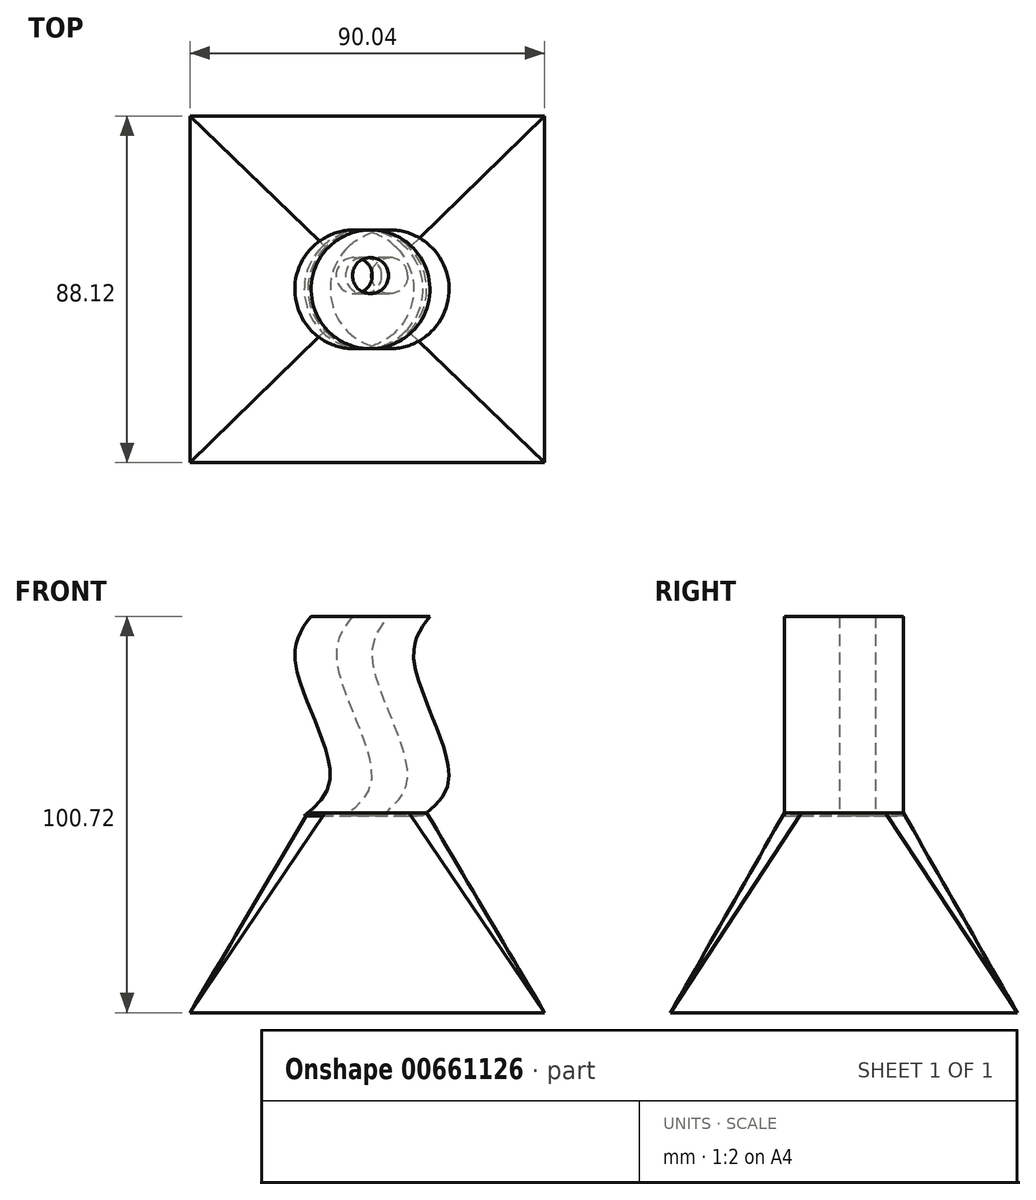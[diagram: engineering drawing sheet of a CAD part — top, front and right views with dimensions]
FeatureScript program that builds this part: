
annotation { "Feature Type Name" : "Feature", "Feature Type Description" : "" }
export const myFeature = defineFeature(function(context is Context, id is Id, definition is map)
    precondition{}
    {
        {
            var Q0;
            Q0=qCreatedBy(makeId("Top.planeOp"),FACE);
            cPlane(context, id + "F0", {"entities" : qUnion([Q0]), "cplaneType" : CPlaneType.OFFSET, "offset" : 50.8 * mm, "width" : 152.4 * mm, "height" : 152.4 * mm});
        }
        {
            var Q0;
            Q0=qCreatedBy(makeId("Top.planeOp"),FACE);
            var sketch = newSketch(context, id + "F1", { "sketchPlane" : qUnion([Q0])});
            skLineSegment(sketch, "E0.bottom", {"start": v(45.02, 44.06) * mm, "end": v(-45.02, 44.06) * mm});
            skLineSegment(sketch, "E0.top", {"start": v(45.02, -44.06) * mm, "end": v(-45.02, -44.06) * mm});
            skLineSegment(sketch, "E0.left", {"start": v(45.02, 44.06) * mm, "end": v(45.02, -44.06) * mm});
            skLineSegment(sketch, "E0.right", {"start": v(-45.02, 44.06) * mm, "end": v(-45.02, -44.06) * mm});
            skPoint(sketch, "E0.middle", {"position": v(0, 0) * mm});
            skSolve(sketch);
        }
        {
            var Q0;
            Q0=qCreatedBy(id+"F0.planeOp",FACE);
            var sketch = newSketch(context, id + "F2", { "sketchPlane" : qUnion([Q0])});
            skCircle(sketch, "E1", {"center": v(0, 0) * mm, "radius": 15.1 * mm});
            skSolve(sketch);
        }
        {
            var Q0;
            Q0=makeQuery(id+"F1.imprint","IMPRINT",FACE,{"disambiguationData":[TD([[makeQuery(id+"F1.imprint","IMPRINT",EDGE,{"derivedFrom":sQuery(id+"F1.wireOp",EDGE,"E0.bottom")}),1.0]])]});
            var Q1;
            Q1=makeQuery(id+"F2.imprint","IMPRINT",FACE,{"disambiguationData":[TD([[makeQuery(id+"F2.imprint","IMPRINT",EDGE,{"derivedFrom":sQuery(id+"F2.wireOp",EDGE,"E1")}),1.0]])]});
            loft(context, id + "F3", {"sheetProfilesArray" : [{ "sheetProfileEntities" : qUnion([Q0]) }, { "sheetProfileEntities" : qUnion([Q1]) }]});
        }
        {
            var Q0;
            Q0=qCreatedBy(makeId("Front.planeOp"),FACE);
            var sketch = newSketch(context, id + "F4", { "sketchPlane" : qUnion([Q0])});
            skFitSpline(sketch, "E2", {"points": [v(0, 50.04) * mm, v(6.6, 60.36) * mm, v(-2.32, 89.52) * mm, v(1.74, 100.72) * mm], "startDerivative": vector(35.2, 28.9) * mm, "endDerivative": vector(24.91, 33.2) * mm});
            skSolve(sketch);
        }
        {
            var Q0;
            Q0=makeQuery(id+"F3.opLoft","CAP_FACE",FACE,{"disambiguationData":[OSD([makeQuery(id+"F2.imprint","IMPRINT",FACE,{"disambiguationData":[TD([[makeQuery(id+"F2.imprint","IMPRINT",EDGE,{"derivedFrom":sQuery(id+"F2.wireOp",EDGE,"E1")}),1.0]])]})])],"isStart":true});
            var sketch = newSketch(context, id + "F5", { "sketchPlane" : qUnion([Q0])});
            skCircle(sketch, "E3", {"center": v(0, 3.49) * mm, "radius": 4.59 * mm});
            skSolve(sketch);
        }
        {
            var Q0;
            Q0=makeQuery(id+"F5.imprint","IMPRINT",FACE,{"disambiguationData":[TD([[makeQuery(id+"F5.imprint","IMPRINT",EDGE,{"derivedFrom":sQuery(id+"F5.wireOp",EDGE,"E3")}),-1.0]])]});
            var Q1;
            Q1=sQuery(id+"F4.wireOp",EDGE,"E2");
            sweep(context, id + "F6", {"profiles" : qUnion([Q0]), "path" : qUnion([Q1]), "keepProfileOrientation" : true});
        }
    });
